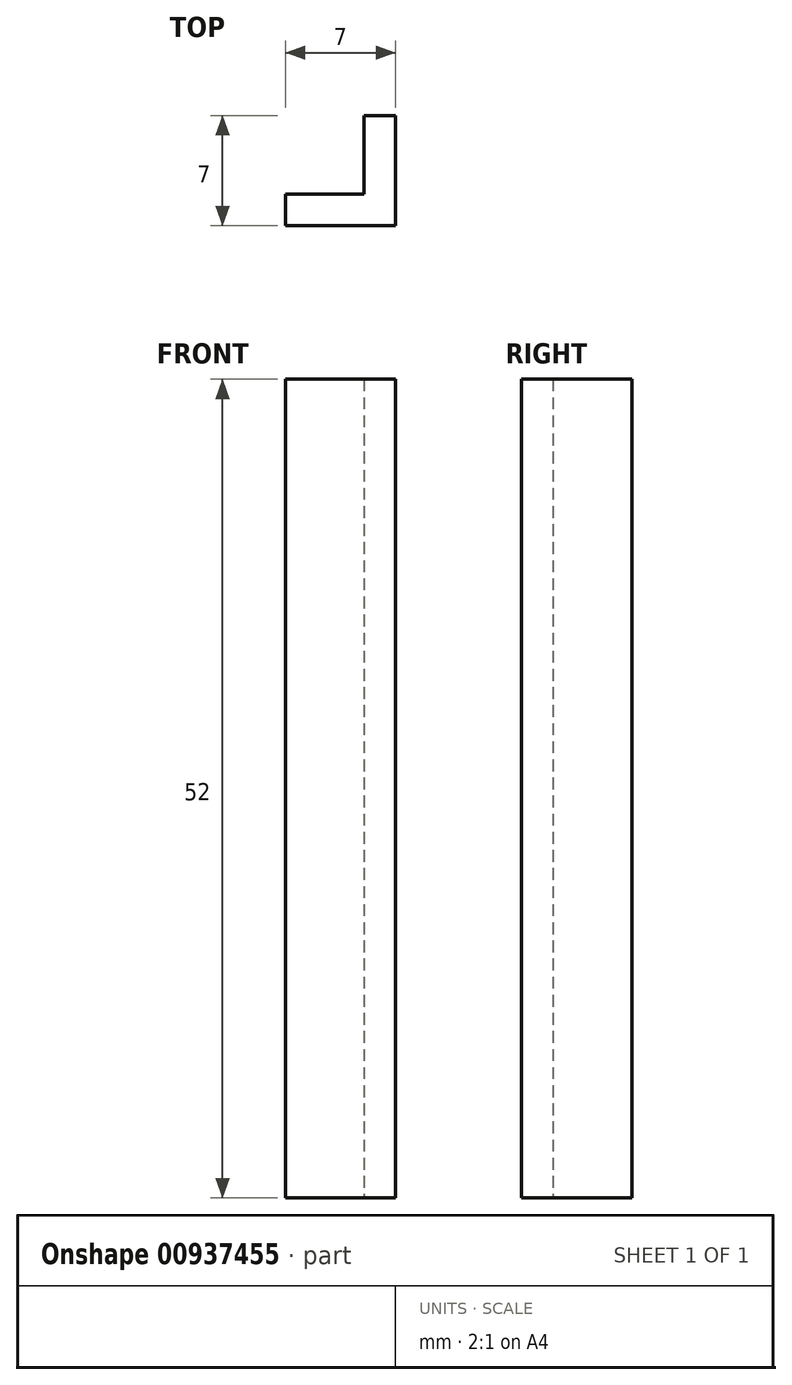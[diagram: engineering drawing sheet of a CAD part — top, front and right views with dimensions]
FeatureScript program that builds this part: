
annotation { "Feature Type Name" : "Feature", "Feature Type Description" : "" }
export const myFeature = defineFeature(function(context is Context, id is Id, definition is map)
    precondition{}
    {
        {
            var Q0;
            Q0=qCreatedBy(makeId("Top.planeOp"),FACE);
            var sketch = newSketch(context, id + "F0", { "sketchPlane" : qUnion([Q0])});
            skLineSegment(sketch, "E0", {"start": v(0, 0) * mm, "end": v(-7, 0) * mm});
            skLineSegment(sketch, "E1", {"start": v(-7, 0) * mm, "end": v(-7, 2) * mm});
            skLineSegment(sketch, "E2", {"start": v(-7, 2) * mm, "end": v(-2, 2) * mm});
            skLineSegment(sketch, "E3", {"start": v(-2, 2) * mm, "end": v(-2, 7) * mm});
            skLineSegment(sketch, "E4", {"start": v(-2, 7) * mm, "end": v(0, 7) * mm});
            skLineSegment(sketch, "E5", {"start": v(0, 7) * mm, "end": v(0, 0) * mm});
            skSolve(sketch);
        }
        {
            var Q0;
            Q0=makeQuery(id+"F0.imprint","IMPRINT",FACE,{"disambiguationData":[TD([[makeQuery(id+"F0.imprint","IMPRINT",EDGE,{"derivedFrom":sQuery(id+"F0.wireOp",EDGE,"E0")}),-1.0]])]});
            extrude(context, id + "F1", {"entities" : qUnion([Q0]), "depth" : (26 * 2) * mm, "offsetDistance" : 25 * mm});
        }
    });
